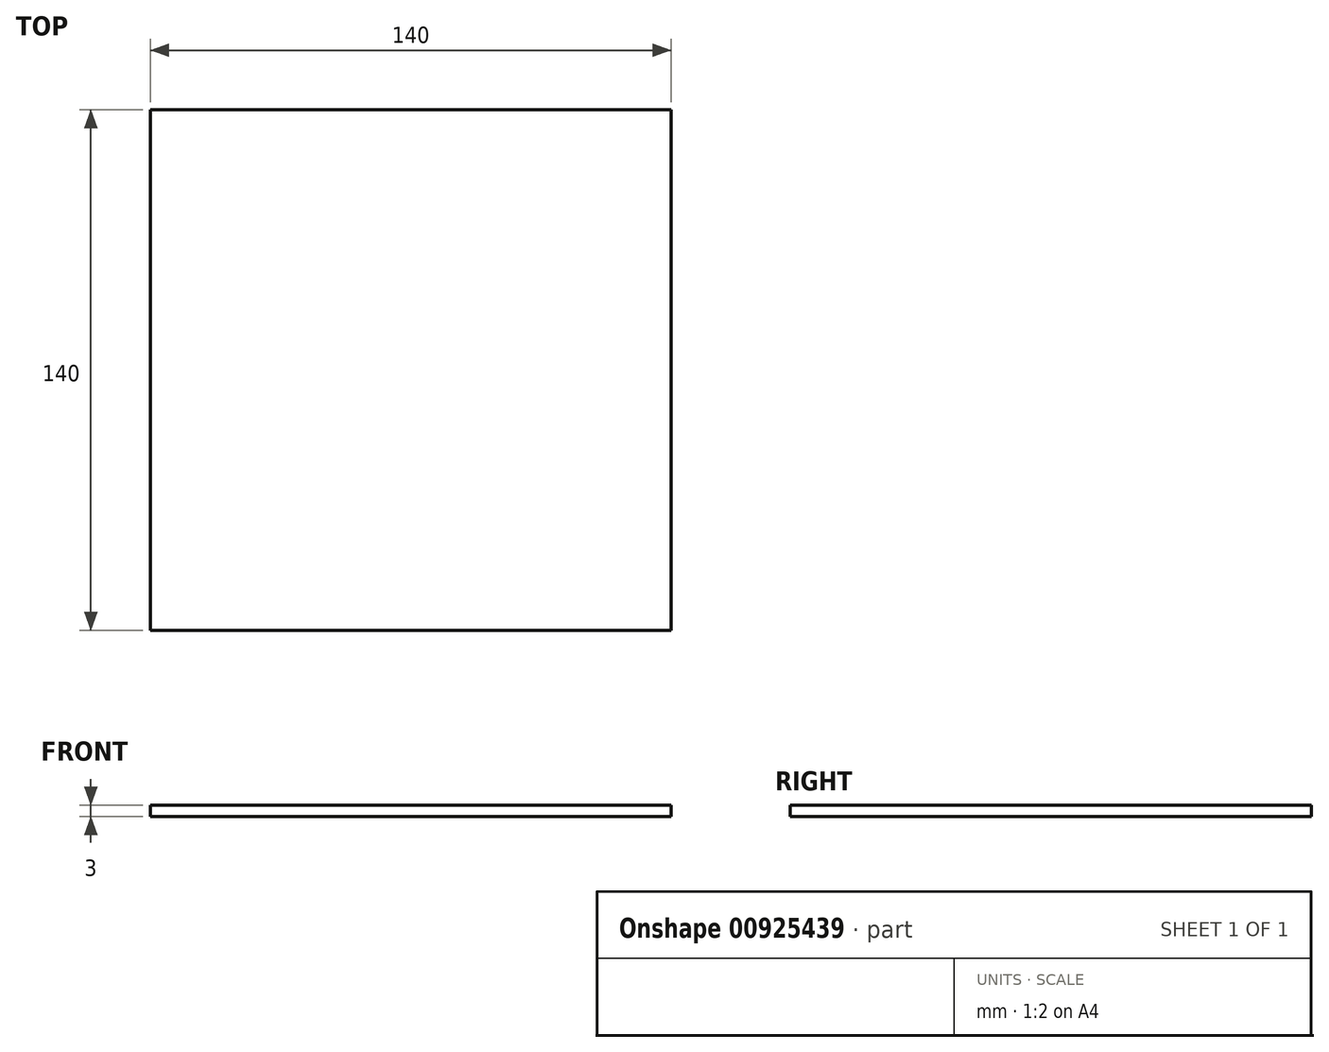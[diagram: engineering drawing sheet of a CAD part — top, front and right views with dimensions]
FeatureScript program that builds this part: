
annotation { "Feature Type Name" : "Feature", "Feature Type Description" : "" }
export const myFeature = defineFeature(function(context is Context, id is Id, definition is map)
    precondition{}
    {
        {
            var Q0;
            Q0=qCreatedBy(makeId("Top.planeOp"),FACE);
            var sketch = newSketch(context, id + "F0", { "sketchPlane" : qUnion([Q0])});
            skLineSegment(sketch, "E0.bottom", {"start": v(-70, 70) * mm, "end": v(70, 70) * mm});
            skLineSegment(sketch, "E0.top", {"start": v(-70, -70) * mm, "end": v(70, -70) * mm});
            skLineSegment(sketch, "E0.left", {"start": v(-70, 70) * mm, "end": v(-70, -70) * mm});
            skLineSegment(sketch, "E0.right", {"start": v(70, 70) * mm, "end": v(70, -70) * mm});
            skPoint(sketch, "E0.middle", {"position": v(0, 0) * mm});
            skSolve(sketch);
        }
        {
            var Q0;
            Q0 = qSketchRegion(id + "F0", true);
            extrude(context, id + "F1", {"entities" : qUnion([Q0]), "depth" : 3 * mm, "offsetDistance" : 25 * mm});
        }
    });
